FCSTD DOCUMENT  (FreeCAD 0.20R29177 (Git))
Label: Vesa10Pouces
License: All rights reserved
LicenseURL: http://en.wikipedia.org/wiki/All_rights_reserved
objects: Sketcher::SketchObject×1, PartDesign::Body×1
note: 2 computed .brp shape members not serialized (recipe doc carries the construction recipe); baked Part::Feature solids carry a one-line shape summary decoded from their .brp
EXTERNAL_REF file=DonneesBoitier.FCStd obj=Spreadsheet

FEATURE [Sketcher::SketchObject] Sketch
  FullyConstrained = true
  MapMode = 5
  Support = -> [XY_Plane]
  expr: Constraints[11] = <<DonneesBoitier>>#<<Spreadsheet>>.xxVesa
  expr: Constraints[124] = <<DonneesBoitier>>#<<Spreadsheet>>.xxLargEconche
  expr: Constraints[125] = <<DonneesBoitier>>#<<Spreadsheet>>.xxLargEconche
  expr: Constraints[126] = <<DonneesBoitier>>#<<Spreadsheet>>.xxLargEconche
  expr: Constraints[14] = <<DonneesBoitier>>#<<Spreadsheet>>.xxVesa
  expr: Constraints[16] = <<DonneesBoitier>>#Spreadsheet.xxLongDessus
  expr: Constraints[17] = <<DonneesBoitier>>#<<Spreadsheet>>.xxHauteurEncasEcran
  expr: Constraints[18] = <<DonneesBoitier>>#<<Spreadsheet>>.xxLargEconche
  expr: Constraints[19] = <<DonneesBoitier>>#<<Spreadsheet>>.xxLargEconche
  expr: Constraints[20] = <<DonneesBoitier>>#<<Spreadsheet>>.xxEspaceTrouEncoche
  expr: Constraints[23] = <<DonneesBoitier>>#Spreadsheet.xxLongDessus
  expr: Constraints[36] = <<DonneesBoitier>>#Spreadsheet.xxLongEncoches
  expr: Constraints[72] = <<DonneesBoitier>>#<<Spreadsheet>>.xxEspaceTrouEncoche * 2
  expr: Constraints[74] = <<DonneesBoitier>>#<<Spreadsheet>>.xxLargEconche
  expr: Constraints[75] = <<DonneesBoitier>>#<<Spreadsheet>>.xxLargEconche
  expr: Constraints[89] = <<DonneesBoitier>>#<<Spreadsheet>>.xxLargEconche
  sketch-geometry (57):
    g0: LineSegment StartX=97.5 StartY=131.5 StartZ=0 EndX=-97.5 EndY=131.5 EndZ=0
    g1: LineSegment StartX=-97.5 StartY=-131.5 StartZ=0 EndX=97.5 EndY=-131.5 EndZ=0
    g2: GeomPoint X=0 Y=0 Z=0
    g3: Circle CenterX=-37.5 CenterY=37.5 CenterZ=0 NormalX=0 NormalY=0 NormalZ=1 AngleXU=0 Radius=2.5
    g4: Circle CenterX=-37.5 CenterY=-37.5 CenterZ=0 NormalX=0 NormalY=0 NormalZ=1 AngleXU=0 Radius=2.5
    g5: Circle CenterX=37.5 CenterY=37.5 CenterZ=0 NormalX=0 NormalY=0 NormalZ=1 AngleXU=0 Radius=2.5
    g6: Circle CenterX=37.5 CenterY=-37.5 CenterZ=0 NormalX=0 NormalY=0 NormalZ=1 AngleXU=0 Radius=2.5
    g7: LineSegment StartX=97.5 StartY=-15 StartZ=0 EndX=97.5 EndY=15 EndZ=0
    g8: LineSegment StartX=97.5 StartY=30 StartZ=0 EndX=102.5 EndY=30 EndZ=0
    g9: LineSegment StartX=102.5 StartY=30 StartZ=0 EndX=102.5 EndY=15 EndZ=0
    g10: LineSegment StartX=102.5 StartY=15 StartZ=0 EndX=97.5 EndY=15 EndZ=0
    g11: LineSegment StartX=97.5 StartY=-15 StartZ=0 EndX=102.5 EndY=-15 EndZ=0
    g12: LineSegment StartX=102.5 StartY=-15 StartZ=0 EndX=102.5 EndY=-30 EndZ=0
    g13: LineSegment StartX=102.5 StartY=-30 StartZ=0 EndX=97.5 EndY=-30 EndZ=0
    g14: LineSegment StartX=-97.5 StartY=15 StartZ=0 EndX=-97.5 EndY=-15 EndZ=0
    g15: LineSegment StartX=-97.5 StartY=30 StartZ=0 EndX=-102.5 EndY=30 EndZ=0
    g16: LineSegment StartX=-102.5 StartY=30 StartZ=0 EndX=-102.5 EndY=15 EndZ=0
    g17: LineSegment StartX=-102.5 StartY=15 StartZ=0 EndX=-97.5 EndY=15 EndZ=0
    g18: LineSegment StartX=-97.5 StartY=-15 StartZ=0 EndX=-102.5 EndY=-15 EndZ=0
    g19: LineSegment StartX=-102.5 StartY=-15 StartZ=0 EndX=-102.5 EndY=-30 EndZ=0
    g20: LineSegment StartX=-102.5 StartY=-30 StartZ=0 EndX=-97.5 EndY=-30 EndZ=0
    g21: LineSegment StartX=97.5 StartY=-60 StartZ=0 EndX=97.5 EndY=-30 EndZ=0
    g22: LineSegment StartX=97.5 StartY=-105 StartZ=0 EndX=97.5 EndY=-75 EndZ=0
    g23: LineSegment StartX=97.5 StartY=-131.5 StartZ=0 EndX=97.5 EndY=-120 EndZ=0
    g24: LineSegment StartX=97.5 StartY=30 StartZ=0 EndX=97.5 EndY=60 EndZ=0
    g25: LineSegment StartX=97.5 StartY=75 StartZ=0 EndX=97.5 EndY=105 EndZ=0
    g26: LineSegment StartX=97.5 StartY=120 StartZ=0 EndX=97.5 EndY=131.5 EndZ=0
    g27: LineSegment StartX=-97.5 StartY=60 StartZ=0 EndX=-97.5 EndY=30 EndZ=0
    g28: LineSegment StartX=-97.5 StartY=105 StartZ=0 EndX=-97.5 EndY=75 EndZ=0
    g29: LineSegment StartX=-97.5 StartY=131.5 StartZ=0 EndX=-97.5 EndY=120 EndZ=0
    g30: LineSegment StartX=-97.5 StartY=-30 StartZ=0 EndX=-97.5 EndY=-60 EndZ=0
    g31: LineSegment StartX=-97.5 StartY=-75 StartZ=0 EndX=-97.5 EndY=-105 EndZ=0
    g32: LineSegment StartX=-97.5 StartY=-120 StartZ=0 EndX=-97.5 EndY=-131.5 EndZ=0
    g33: LineSegment StartX=97.5 StartY=-60 StartZ=0 EndX=102.5 EndY=-60 EndZ=0
    g34: LineSegment StartX=102.5 StartY=-60 StartZ=0 EndX=102.5 EndY=-75 EndZ=0
    g35: LineSegment StartX=102.5 StartY=-75 StartZ=0 EndX=97.5 EndY=-75 EndZ=0
    g36: LineSegment StartX=97.5 StartY=-105 StartZ=0 EndX=102.5 EndY=-105 EndZ=0
    g37: LineSegment StartX=102.5 StartY=-105 StartZ=0 EndX=102.5 EndY=-120 EndZ=0
    g38: LineSegment StartX=102.5 StartY=-120 StartZ=0 EndX=97.5 EndY=-120 EndZ=0
    g39: LineSegment StartX=97.5 StartY=75 StartZ=0 EndX=102.5 EndY=75 EndZ=0
    g40: LineSegment StartX=102.5 StartY=75 StartZ=0 EndX=102.5 EndY=60 EndZ=0
    g41: LineSegment StartX=102.5 StartY=60 StartZ=0 EndX=97.5 EndY=60 EndZ=0
    g42: LineSegment StartX=97.5 StartY=120 StartZ=0 EndX=102.5 EndY=120 EndZ=0
    g43: LineSegment StartX=102.5 StartY=120 StartZ=0 EndX=102.5 EndY=105 EndZ=0
    g44: LineSegment StartX=102.5 StartY=105 StartZ=0 EndX=97.5 EndY=105 EndZ=0
    g45: LineSegment StartX=-102.5 StartY=60 StartZ=0 EndX=-97.5 EndY=60 EndZ=0
    g46: LineSegment StartX=-102.5 StartY=75 StartZ=0 EndX=-102.5 EndY=60 EndZ=0
    g47: LineSegment StartX=-97.5 StartY=75 StartZ=0 EndX=-102.5 EndY=75 EndZ=0
    g48: LineSegment StartX=-102.5 StartY=105 StartZ=0 EndX=-97.5 EndY=105 EndZ=0
    g49: LineSegment StartX=-102.5 StartY=120 StartZ=0 EndX=-102.5 EndY=105 EndZ=0
    g50: LineSegment StartX=-97.5 StartY=120 StartZ=0 EndX=-102.5 EndY=120 EndZ=0
    g51: LineSegment StartX=-97.5 StartY=-60 StartZ=0 EndX=-102.5 EndY=-60 EndZ=0
    g52: LineSegment StartX=-102.5 StartY=-60 StartZ=0 EndX=-102.5 EndY=-75 EndZ=0
    g53: LineSegment StartX=-102.5 StartY=-75 StartZ=0 EndX=-97.5 EndY=-75 EndZ=0
    g54: LineSegment StartX=-97.5 StartY=-105 StartZ=0 EndX=-102.5 EndY=-105 EndZ=0
    g55: LineSegment StartX=-102.5 StartY=-105 StartZ=0 EndX=-102.5 EndY=-120 EndZ=0
    g56: LineSegment StartX=-102.5 StartY=-120 StartZ=0 EndX=-97.5 EndY=-120 EndZ=0
  constraints (162):
    c: Coincident(g26,g0)
    c: Coincident(g0,g29)
    c: Coincident(g32,g1)
    c: Coincident(g1,g23)
    c: Horizontal(g0)
    c: Symmetric(g0,g23,g2)
    c: Coincident(g2,g-1)
    c: Equal(g3,g5)
    c: Equal(g3,g6)
    c: Equal(g3,g4)
    c: Diameter(g3) = 5
    c: DistanceX(g3,g5) = 75
    c: Symmetric(g3,g5,g-2)
    c: Symmetric(g4,g6,g-2)
    c: DistanceY(g4,g3) = 75
    c: Symmetric(g4,g3,g-1)
    c: DistanceX(g0,g0) = 195
    c: DistanceY(g32,g29) = 263
    c: DistanceY(g7,g24) = 15
    c: DistanceY(g21,g7) = 15
    c: DistanceY(g-1,g7) = 15
    c: Symmetric(g7,g7,g-1)
    c: Equal(g0,g1)
    c: DistanceX(g0,g7) = 195
    c: Coincident(g24,g8)
    c: Horizontal(g8)
    c: Coincident(g8,g9)
    c: Vertical(g9)
    c: Coincident(g9,g10)
    c: Horizontal(g10)
    c: Horizontal(g11)
    c: Coincident(g11,g12)
    c: Vertical(g12)
    c: Coincident(g12,g13)
    c: Coincident(g13,g21)
    c: Horizontal(g13)
    c: Distance(g8) = 5
    c: Equal(g8,g11)
    c: Coincident(g11,g7)
    c: Coincident(g10,g7)
    c: Vertical(g14)
    c: Equal(g7,g14)
    c: Symmetric(g1,g1,g-2)
    c: Symmetric(g14,g7,g-2)
    c: Horizontal(g15)
    c: Coincident(g15,g16)
    c: Vertical(g16)
    c: Coincident(g16,g17)
    c: Coincident(g17,g14)
    c: Horizontal(g17)
    c: Coincident(g14,g18)
    c: Horizontal(g18)
    c: Coincident(g18,g19)
    c: Vertical(g19)
    c: Coincident(g19,g20)
    c: Coincident(g20,g30)
    c: Equal(g17,g18)
    c: Equal(g18,g20)
    c: Equal(g20,g11)
    c: Coincident(g15,g27)
    c: Vertical(g21)
    c: Vertical(g22)
    c: Vertical(g23)
    c: Vertical(g24)
    c: Vertical(g25)
    c: Vertical(g26)
    c: Vertical(g27)
    c: Vertical(g28)
    c: Vertical(g29)
    c: Vertical(g30)
    c: Vertical(g31)
    c: Vertical(g32)
    c: DistanceY(g8,g24) = 30
    c: Equal(g25,g24)
    c: DistanceY(g25,g26) = 15
    c: DistanceY(g24,g25) = 15
    c: Equal(g21,g24)
    c: Equal(g22,g21)
    c: DistanceX(g26,g25) = 0
    c: DistanceX(g25,g24) = 0
    c: DistanceX(g13,g7) = 0
    c: DistanceX(g22,g21) = 0
    c: Horizontal(g33)
    c: Coincident(g33,g34)
    c: Vertical(g34)
    c: Coincident(g34,g35)
    c: Horizontal(g35)
    c: Coincident(g35,g22)
    c: Equal(g12,g34)
    c: DistanceY(g23,g22) = 15
    c: Coincident(g33,g21)
    c: Equal(g13,g33)
    c: Horizontal(g36)
    c: Coincident(g36,g37)
    c: Vertical(g37)
    c: Coincident(g37,g38)
    c: Horizontal(g38)
    c: Coincident(g36,g22)
    c: Coincident(g38,g23)
    c: Equal(g35,g36)
    c: Horizontal(g39)
    c: Coincident(g39,g40)
    c: Vertical(g40)
    c: Coincident(g40,g41)
    c: Horizontal(g41)
    c: Distance(g39) = 5
    c: Coincident(g39,g25)
    c: Coincident(g41,g24)
    c: Horizontal(g42)
    c: Coincident(g42,g43)
    c: Vertical(g43)
    c: Coincident(g43,g44)
    c: Horizontal(g44)
    c: Distance(g42) = 5
    c: Coincident(g42,g26)
    c: Coincident(g44,g25)
    c: Equal(g29,g26)
    c: Equal(g25,g28)
    c: Equal(g27,g24)
    c: Equal(g16,g9)
    c: Equal(g19,g12)
    c: Equal(g30,g21)
    c: Equal(g31,g22)
    c: Equal(g32,g23)
    c: DistanceY(g32,g31) = 15
    c: DistanceY(g31,g30) = 15
    c: DistanceY(g27,g28) = 15
    c: DistanceX(g31,g30) = 0
    c: DistanceX(g29,g28) = 0
    c: DistanceX(g27,g28) = 0
    c: Horizontal(g47)
    c: Coincident(g47,g46)
    c: Vertical(g46)
    c: Coincident(g46,g45)
    c: Horizontal(g45)
    c: Coincident(g47,g28)
    c: Coincident(g45,g27)
    c: Equal(g45,g15)
    c: Horizontal(g50)
    c: Coincident(g50,g49)
    c: Vertical(g49)
    c: Coincident(g49,g48)
    c: Horizontal(g48)
    c: Coincident(g50,g29)
    c: Coincident(g48,g28)
    c: Equal(g47,g48)
    c: Horizontal(g51)
    c: Coincident(g51,g52)
    c: Vertical(g52)
    c: Coincident(g52,g53)
    c: Equal(g51,g53)
    c: Coincident(g53,g31)
    c: Coincident(g51,g30)
    c: Equal(g51,g20)
    c: Horizontal(g54)
    c: Coincident(g54,g55)
    c: Vertical(g55)
    c: Coincident(g55,g56)
    c: Equal(g54,g56)
    c: Coincident(g56,g32)
    c: Coincident(g54,g31)
    c: Equal(g54,g53)
FEATURE [PartDesign::Body] Body
  Group = -> [Sketch]
  Origin = -> Origin
